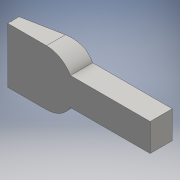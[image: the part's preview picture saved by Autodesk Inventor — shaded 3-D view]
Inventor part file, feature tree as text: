
AUTODESK INVENTOR PART (.ipt)
format: ipt  version: 2016 (Build 200138000, 138)  size: 124,928 bytes
history: native  units: mm
features: extrude x3, sketch x3, chamfer x2, plane x1
ambient origin geometry x8: Origin, YZ Plane, XZ Plane, XY Plane, X Axis, Y Axis, Z Axis, Center Point
bodies: Solid1 (feature_tree)
feature tree (9):
  extrude  "Extrusion1"  Depth=4.0mm
  chamfer  "Chamfer1"  Distance=4.0mm
  plane  "Work Plane1"
  extrude  "Extrusion2"  Depth=10.0mm
  extrude  "Extrusion3"  Depth=5.0mm
  chamfer  "Chamfer3"  Distance=15.0mm
  sketch  "Sketch1"  dims[d0=10.0mm d2=7.0mm d3=4.0mm d4=0.0mm]
  sketch  "Sketch3"  dims[d5=10.0mm d6=2.0mm d7=1.919862mm d18=1.745329mm]
  sketch  "Sketch4"  dims[d19=3.0mm d20=0.0mm d24=5.0mm d25=15.0mm d26=4.0mm d27=0.0mm d30=10.0mm d31=2.0mm d32=0.349066mm]
